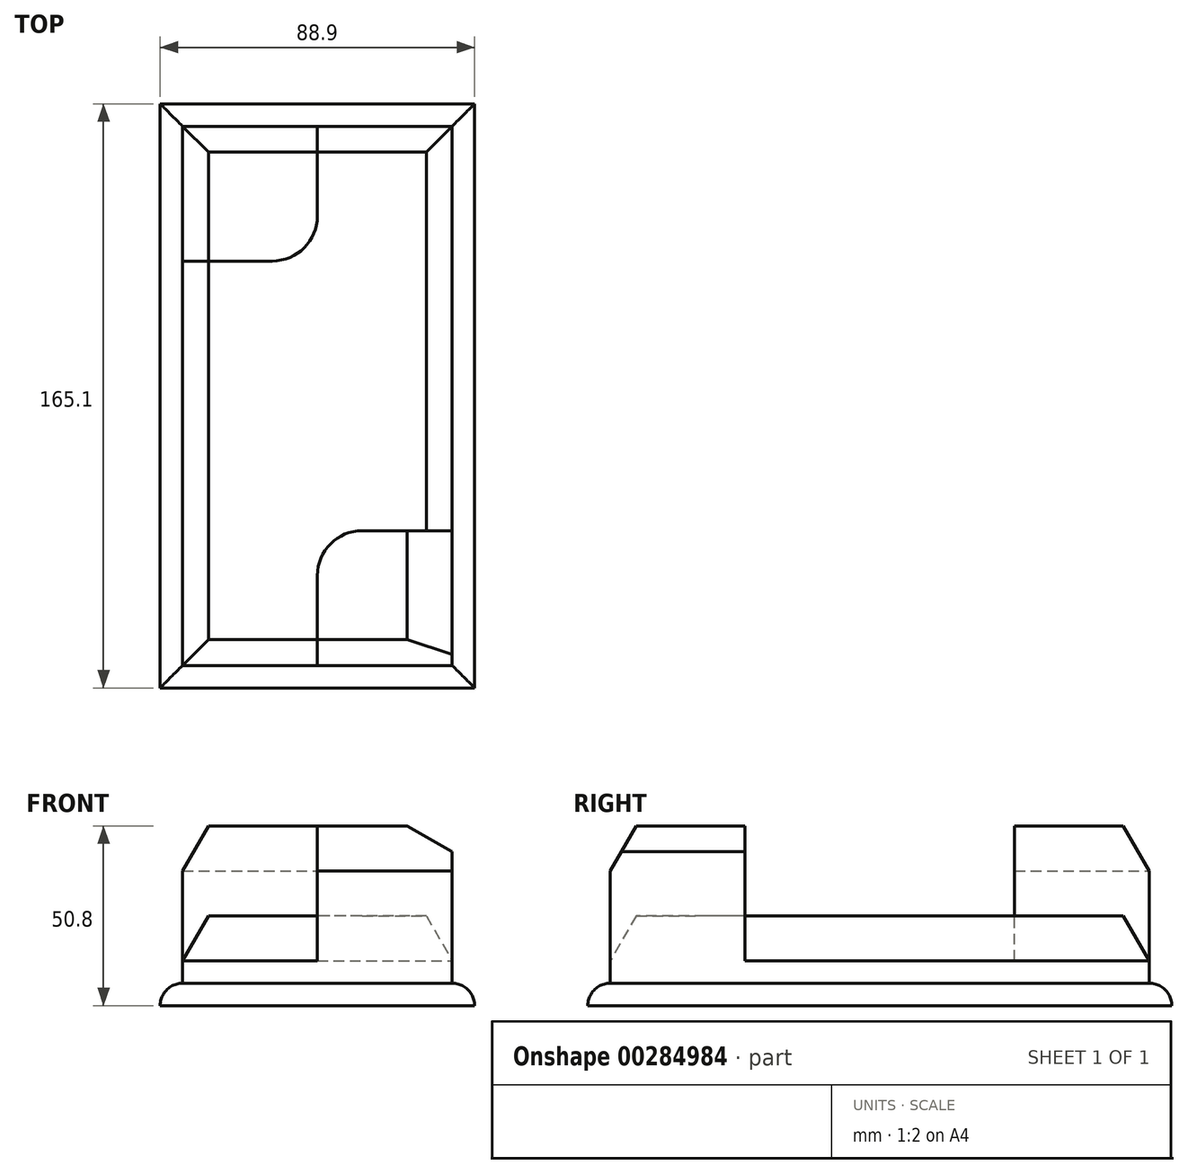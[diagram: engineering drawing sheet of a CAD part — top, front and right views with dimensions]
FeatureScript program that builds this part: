
annotation { "Feature Type Name" : "Feature", "Feature Type Description" : "" }
export const myFeature = defineFeature(function(context is Context, id is Id, definition is map)
    precondition{}
    {
        {
            var Q0;
            Q0=qCreatedBy(makeId("Top.planeOp"),FACE);
            var sketch = newSketch(context, id + "F0", { "sketchPlane" : qUnion([Q0])});
            skLineSegment(sketch, "E0.bottom", {"start": v(-38.1, 76.2) * mm, "end": v(38.1, 76.2) * mm});
            skLineSegment(sketch, "E0.top", {"start": v(-38.1, -76.2) * mm, "end": v(38.1, -76.2) * mm});
            skLineSegment(sketch, "E0.left", {"start": v(-38.1, 76.2) * mm, "end": v(-38.1, -76.2) * mm});
            skLineSegment(sketch, "E0.right", {"start": v(38.1, 76.2) * mm, "end": v(38.1, -76.2) * mm});
            skPoint(sketch, "E0.middle", {"position": v(0, 0) * mm});
            skLineSegment(sketch, "E1.bottom", {"start": v(-44.45, 82.55) * mm, "end": v(44.45, 82.55) * mm});
            skLineSegment(sketch, "E1.top", {"start": v(-44.45, -82.55) * mm, "end": v(44.45, -82.55) * mm});
            skLineSegment(sketch, "E1.left", {"start": v(-44.45, 82.55) * mm, "end": v(-44.45, -82.55) * mm});
            skLineSegment(sketch, "E1.right", {"start": v(44.45, 82.55) * mm, "end": v(44.45, -82.55) * mm});
            skPoint(sketch, "E2.oppositeSnap0", {"position": v(0, 76.2) * mm});
            skLineSegment(sketch, "E3", {"start": v(0, 76.2) * mm, "end": v(0, 50.8) * mm});
            skLineSegment(sketch, "E4", {"start": v(-12.7, 38.1) * mm, "end": v(-38.1, 38.1) * mm});
            skPoint(sketch, "E5.visualSharp", {"position": v(0, 38.1) * mm});
            skArc(sketch, "E5.filletArc", {"start": v(-12.7, 38.1) * mm, "mid": v(-3.72, 41.82) * mm, "end": v(0, 50.8) * mm});
            skLineSegment(sketch, "E6", {"start": v(0, -76.2) * mm, "end": v(0, -50.8) * mm});
            skPoint(sketch, "E6.endSnap0", {"position": v(0, -76.2) * mm});
            skLineSegment(sketch, "E7", {"start": v(12.7, -38.1) * mm, "end": v(38.1, -38.1) * mm});
            skPoint(sketch, "E8.visualSharp", {"position": v(0, -38.1) * mm});
            skArc(sketch, "E8.filletArc", {"start": v(12.7, -38.1) * mm, "mid": v(3.72, -41.82) * mm, "end": v(0, -50.8) * mm});
            skSolve(sketch);
        }
        {
            var Q0;
            Q0=makeQuery(id+"F0.imprint","IMPRINT",FACE,{"disambiguationData":[TD([[makeQuery(id+"F0.imprint","IMPRINT",EDGE,{"derivedFrom":sQuery(id+"F0.wireOp",EDGE,"E1.bottom")}),-1.0]])]});
            extrude(context, id + "F1", {"entities" : qUnion([Q0]), "depth" : 6.35 * mm});
        }
        {
            var Q0;
            Q0=makeQuery(id+"F1.opExtrude","CAP_EDGE",EDGE,{"disambiguationData":[OSD([sQuery(id+"F0.wireOp",EDGE,"E1.left")])],"isStart":false});
            var Q1;
            Q1=makeQuery(id+"F1.opExtrude","CAP_EDGE",EDGE,{"disambiguationData":[OSD([sQuery(id+"F0.wireOp",EDGE,"E1.top")])],"isStart":false});
            var Q2;
            Q2=makeQuery(id+"F1.opExtrude","CAP_EDGE",EDGE,{"disambiguationData":[OSD([sQuery(id+"F0.wireOp",EDGE,"E1.right")])],"isStart":false});
            var Q3;
            Q3=makeQuery(id+"F1.opExtrude","CAP_EDGE",EDGE,{"disambiguationData":[OSD([sQuery(id+"F0.wireOp",EDGE,"E1.bottom")])],"isStart":false});
            fillet(context, id + "F2", {"entities" : qUnion([Q0, Q1, Q2, Q3]), "radius" : 6.35 * mm, "tangentPropagation" : true, "allowEdgeOverflow" : false});
        }
        {
            var Q0;
            {var subQ9=sQuery(id+"F0.wireOp",EDGE,"E3");Q0=makeQuery(id+"F0.imprint","IMPRINT",FACE,{"disambiguationData":[TD([[makeQuery(id+"F0.imprint","IMPRINT",EDGE,{"derivedFrom":subQ9}),1.0]])]});}
            extrude(context, id + "F3", {"entities" : qUnion([Q0]), "operationType" : NewBodyOperationType.ADD, "depth" : 25.4 * mm});
        }
        {
            var Q0;
            {var subQ1=sQuery(id+"F0.wireOp",EDGE,"E6");Q0=makeQuery(id+"F0.imprint","IMPRINT",FACE,{"disambiguationData":[TD([[makeQuery(id+"F0.imprint","IMPRINT",EDGE,{"derivedFrom":subQ1}),-1.0]])]});}
            var Q1;
            {var subQ1=sQuery(id+"F0.wireOp",EDGE,"E3");Q1=makeQuery(id+"F0.imprint","IMPRINT",FACE,{"disambiguationData":[TD([[makeQuery(id+"F0.imprint","IMPRINT",EDGE,{"derivedFrom":subQ1}),-1.0]])]});}
            extrude(context, id + "F4", {"entities" : qUnion([Q0, Q1]), "operationType" : NewBodyOperationType.ADD, "depth" : 50.8 * mm});
        }
        {
            var Q0;
            Q0=makeQuery(id+"F4.opExtrude","CAP_EDGE",EDGE,{"disambiguationData":[OSD([sQuery(id+"F0.wireOp",EDGE,"E0.left")])],"isStart":false});
            var Q1;
            Q1=makeQuery(id+"F4.opExtrude","CAP_EDGE",EDGE,{"disambiguationData":[OSD([sQuery(id+"F0.wireOp",EDGE,"E0.bottom")])],"isStart":false});
            var Q2;
            Q2=makeQuery(id+"F4.opExtrude","CAP_EDGE",EDGE,{"disambiguationData":[OSD([sQuery(id+"F0.wireOp",EDGE,"E0.top")])],"isStart":false});
            var Q3;
            Q3=makeQuery(id+"F4.opExtrude","CAP_EDGE",EDGE,{"disambiguationData":[OSD([sQuery(id+"F0.wireOp",EDGE,"E0.right")])],"isStart":false});
            chamfer(context, id + "F5", {"entities" : qUnion([Q0, Q1, Q2, Q3]), "chamferType" : ChamferType.OFFSET_ANGLE, "width" : 12.7 * mm, "oppositeDirection" : true, "angle" : 30 * degree, "tangentPropagation" : true});
        }
        {
            var Q0;
            Q0=makeQuery(id+"F3.opExtrude","CAP_EDGE",EDGE,{"disambiguationData":[OSD([sQuery(id+"F0.wireOp",EDGE,"E0.right")])],"isStart":false});
            var Q1;
            Q1=makeQuery(id+"F3.opExtrude","CAP_EDGE",EDGE,{"disambiguationData":[OSD([sQuery(id+"F0.wireOp",EDGE,"E0.bottom")])],"isStart":false});
            var Q2;
            Q2=makeQuery(id+"F3.opExtrude","CAP_EDGE",EDGE,{"disambiguationData":[OSD([sQuery(id+"F0.wireOp",EDGE,"E0.left")])],"isStart":false});
            var Q3;
            Q3=makeQuery(id+"F3.opExtrude","CAP_EDGE",EDGE,{"disambiguationData":[OSD([sQuery(id+"F0.wireOp",EDGE,"E0.top")])],"isStart":false});
            chamfer(context, id + "F6", {"entities" : qUnion([Q0, Q1, Q2, Q3]), "chamferType" : ChamferType.OFFSET_ANGLE, "width" : 12.7 * mm, "oppositeDirection" : false, "angle" : 30 * degree, "tangentPropagation" : true});
        }
    });
